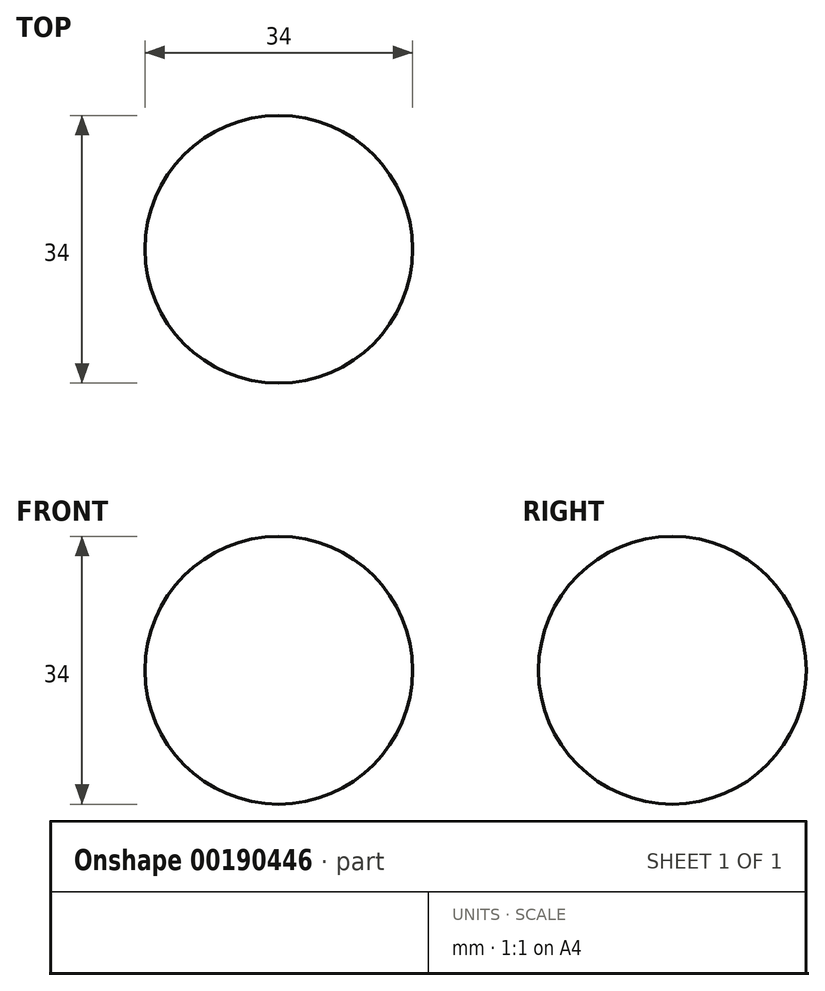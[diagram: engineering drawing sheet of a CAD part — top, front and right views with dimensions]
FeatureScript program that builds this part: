
annotation { "Feature Type Name" : "Feature", "Feature Type Description" : "" }
export const myFeature = defineFeature(function(context is Context, id is Id, definition is map)
    precondition{}
    {
        {
            var Q0;
            Q0=qCreatedBy(makeId("Front.planeOp"),FACE);
            var sketch = newSketch(context, id + "F0", { "sketchPlane" : qUnion([Q0])});
            skArc(sketch, "E0", {"start": v(0, 17) * mm, "mid": v(17, 0) * mm, "end": v(0, -17) * mm});
            skLineSegment(sketch, "E1", {"start": v(0, 17) * mm, "end": v(0, -17) * mm});
            skSolve(sketch);
        }
        {
            var Q0;
            Q0=qSketchRegion(id+"F0",true);
            var Q1;
            Q1=sQuery(id+"F0.wireOp",EDGE,"E1");
            revolve(context, id + "F1", {"entities" : qUnion([Q0]), "axis" : qUnion([Q1]), "revolveType" : RevolveType.FULL});
        }
    });
